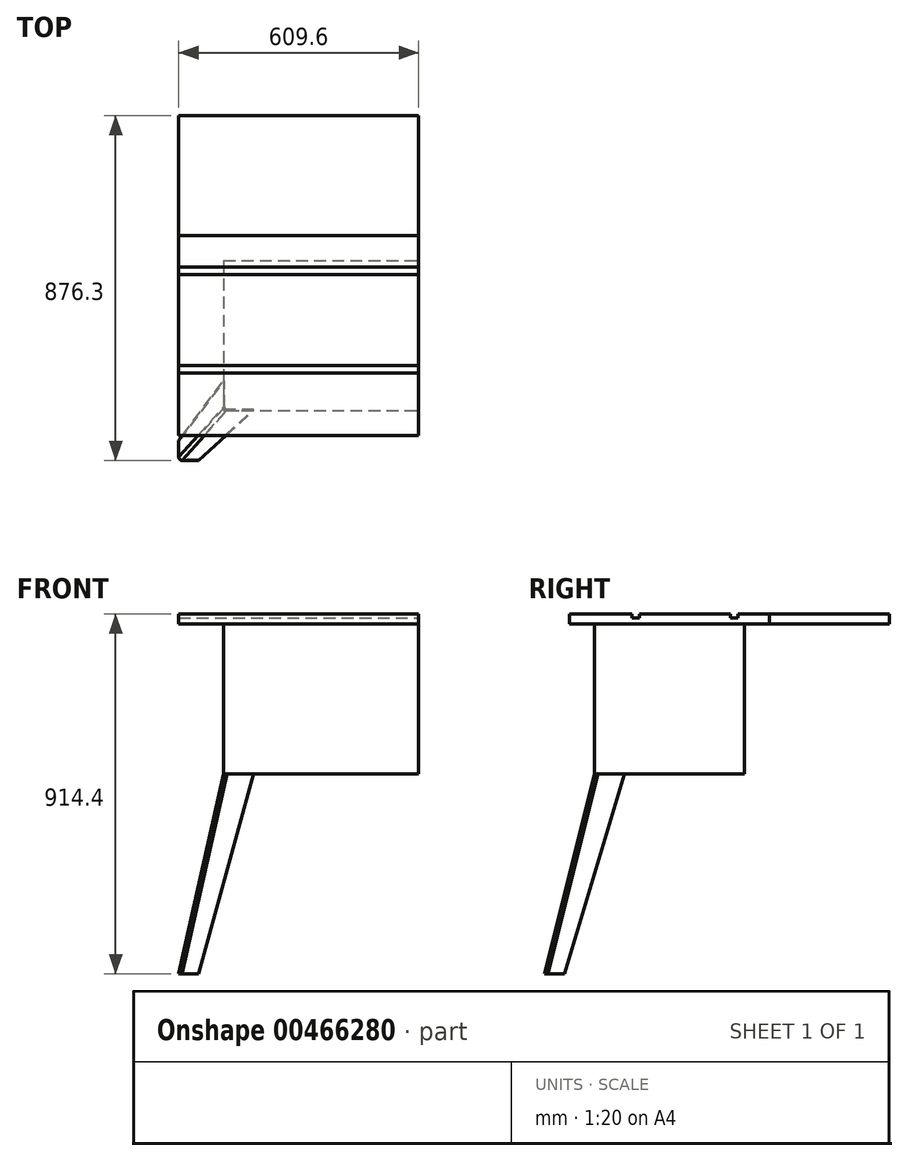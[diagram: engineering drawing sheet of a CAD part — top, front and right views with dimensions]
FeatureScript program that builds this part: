
annotation { "Feature Type Name" : "Feature", "Feature Type Description" : "" }
export const myFeature = defineFeature(function(context is Context, id is Id, definition is map)
    precondition{}
    {
        {
            var Q0;
            Q0=qCreatedBy(makeId("Top.planeOp"),FACE);
            var sketch = newSketch(context, id + "F0", { "sketchPlane" : qUnion([Q0])});
            skLineSegment(sketch, "E0", {"start": v(-361.95, -266.7) * mm, "end": v(-361.95, -308.61) * mm});
            skLineSegment(sketch, "E1", {"start": v(-353.06, -317.5) * mm, "end": v(-311.15, -317.5) * mm});
            skLineSegment(sketch, "E2", {"start": v(-311.15, -317.5) * mm, "end": v(-311.15, -314.96) * mm});
            skLineSegment(sketch, "E3", {"start": v(-311.15, -314.96) * mm, "end": v(-353.06, -314.96) * mm});
            skLineSegment(sketch, "E4", {"start": v(-359.41, -308.61) * mm, "end": v(-359.41, -266.7) * mm});
            skLineSegment(sketch, "E5", {"start": v(-359.41, -266.7) * mm, "end": v(-361.95, -266.7) * mm});
            skPoint(sketch, "E6.visualSharp", {"position": v(-359.41, -314.96) * mm});
            skArc(sketch, "E6.filletArc", {"start": v(-359.41, -308.61) * mm, "mid": v(-357.55, -313.1) * mm, "end": v(-353.06, -314.96) * mm});
            skPoint(sketch, "E7.visualSharp", {"position": v(-361.95, -317.5) * mm});
            skArc(sketch, "E7.filletArc", {"start": v(-361.95, -308.61) * mm, "mid": v(-359.35, -314.9) * mm, "end": v(-353.06, -317.5) * mm});
            skSolve(sketch);
        }
        {
            var Q0;
            Q0=qCreatedBy(makeId("Top.planeOp"),FACE);
            cPlane(context, id + "F1", {"entities" : qUnion([Q0]), "cplaneType" : CPlaneType.OFFSET, "offset" : 508 * mm, "width" : 152.4 * mm, "height" : 152.4 * mm});
        }
        {
            var Q0;
            Q0=qCreatedBy(id+"F1.planeOp",FACE);
            var sketch = newSketch(context, id + "F2", { "sketchPlane" : qUnion([Q0])});
            skPoint(sketch, "E8.middle", {"position": v(0, 0) * mm});
            skLineSegment(sketch, "E9", {"start": v(-247.65, -114.3) * mm, "end": v(-247.65, -181.61) * mm});
            skLineSegment(sketch, "E10", {"start": v(-238.76, -190.5) * mm, "end": v(-171.45, -190.5) * mm});
            skLineSegment(sketch, "E11", {"start": v(-171.45, -190.5) * mm, "end": v(-171.45, -187.96) * mm});
            skLineSegment(sketch, "E12", {"start": v(-171.45, -187.96) * mm, "end": v(-238.76, -187.96) * mm});
            skLineSegment(sketch, "E13", {"start": v(-245.11, -181.61) * mm, "end": v(-245.11, -114.3) * mm});
            skLineSegment(sketch, "E14", {"start": v(-245.11, -114.3) * mm, "end": v(-247.65, -114.3) * mm});
            skPoint(sketch, "E15.visualSharp", {"position": v(-245.11, -187.96) * mm});
            skArc(sketch, "E15.filletArc", {"start": v(-245.11, -181.61) * mm, "mid": v(-243.25, -186.1) * mm, "end": v(-238.76, -187.96) * mm});
            skPoint(sketch, "E16.visualSharp", {"position": v(-247.65, -190.5) * mm});
            skArc(sketch, "E16.filletArc", {"start": v(-247.65, -181.61) * mm, "mid": v(-245.05, -187.9) * mm, "end": v(-238.76, -190.5) * mm});
            skSolve(sketch);
        }
        {
            var Q0;
            Q0=makeQuery(id+"F0.imprint","IMPRINT",FACE,{"disambiguationData":[TD([[makeQuery(id+"F0.imprint","IMPRINT",EDGE,{"derivedFrom":sQuery(id+"F0.wireOp",EDGE,"E0")}),1.0]])]});
            var Q1;
            Q1=makeQuery(id+"F2.imprint","IMPRINT",FACE,{"disambiguationData":[TD([[makeQuery(id+"F2.imprint","IMPRINT",EDGE,{"derivedFrom":sQuery(id+"F2.wireOp",EDGE,"E9")}),1.0]])]});
            loft(context, id + "F3", {"sheetProfilesArray" : [{ "sheetProfileEntities" : qUnion([Q0]) }, { "sheetProfileEntities" : qUnion([Q1]) }]});
        }
        {
            var Q0;
            Q0=qCreatedBy(id+"F1.planeOp",FACE);
            var sketch = newSketch(context, id + "F4", { "sketchPlane" : qUnion([Q0])});
            skLineSegment(sketch, "E17.bottom", {"start": v(-247.65, 190.5) * mm, "end": v(247.65, 190.5) * mm});
            skLineSegment(sketch, "E17.top", {"start": v(-247.65, -190.5) * mm, "end": v(247.65, -190.5) * mm});
            skLineSegment(sketch, "E17.left", {"start": v(-247.65, 190.5) * mm, "end": v(-247.65, -190.5) * mm});
            skLineSegment(sketch, "E17.right", {"start": v(247.65, 190.5) * mm, "end": v(247.65, -190.5) * mm});
            skPoint(sketch, "E17.middle", {"position": v(0, 0) * mm});
            skSolve(sketch);
        }
        {
            var Q0;
            Q0=makeQuery(id+"F4.imprint","IMPRINT",FACE,{"disambiguationData":[TD([[makeQuery(id+"F4.imprint","IMPRINT",EDGE,{"derivedFrom":sQuery(id+"F4.wireOp",EDGE,"E17.bottom")}),-1.0]])]});
            extrude(context, id + "F5", {"entities" : qUnion([Q0]), "depth" : 381 * mm});
        }
        {
            var Q0;
            Q0=makeQuery(id+"F5.opExtrude","CAP_FACE",FACE,{"disambiguationData":[OSD([sQuery(id+"F4.wireOp",EDGE,"E17.bottom"),sQuery(id+"F4.wireOp",EDGE,"E17.top"),sQuery(id+"F4.wireOp",EDGE,"E17.left"),sQuery(id+"F4.wireOp",EDGE,"E17.right")])],"isStart":false});
            var sketch = newSketch(context, id + "F6", { "sketchPlane" : qUnion([Q0])});
            skLineSegment(sketch, "E18.bottom", {"start": v(247.65, 254) * mm, "end": v(-361.95, 254) * mm});
            skLineSegment(sketch, "E18.top", {"start": v(247.65, -254) * mm, "end": v(-361.95, -254) * mm});
            skLineSegment(sketch, "E18.left", {"start": v(247.65, 254) * mm, "end": v(247.65, -254) * mm});
            skLineSegment(sketch, "E18.right", {"start": v(-361.95, 254) * mm, "end": v(-361.95, -254) * mm});
            skLineSegment(sketch, "E19.bottom", {"start": v(-361.95, -254) * mm, "end": v(247.65, -254) * mm});
            skLineSegment(sketch, "E19.top", {"start": v(-361.95, -558.8) * mm, "end": v(247.65, -558.8) * mm});
            skLineSegment(sketch, "E19.left", {"start": v(-361.95, -254) * mm, "end": v(-361.95, -558.8) * mm});
            skLineSegment(sketch, "E19.right", {"start": v(247.65, -254) * mm, "end": v(247.65, -558.8) * mm});
            skLineSegment(sketch, "E20.top", {"start": v(247.65, 558.8) * mm, "end": v(-361.95, 558.8) * mm});
            skLineSegment(sketch, "E20.left", {"start": v(247.65, 254) * mm, "end": v(247.65, 558.8) * mm});
            skLineSegment(sketch, "E20.right", {"start": v(-361.95, 254) * mm, "end": v(-361.95, 558.8) * mm});
            skSolve(sketch);
        }
        {
            var Q0;
            Q0=makeQuery(id+"F6.imprint","IMPRINT",FACE,{"disambiguationData":[TD([[makeQuery(id+"F6.imprint","IMPRINT",EDGE,{"derivedFrom":sQuery(id+"F6.wireOp",EDGE,"E18.right")}),1.0]])]});
            var Q1;
            {var subQ1=makeQuery(id+"F5.opExtrude","CAP_EDGE",EDGE,{"disambiguationData":[OSD([sQuery(id+"F4.wireOp",EDGE,"E17.bottom")])],"isStart":false});Q1=makeQuery(id+"F6.imprint","IMPRINT",FACE,{"disambiguationData":[TD([[makeQuery(id+"F6.imprint","IMPRINT",EDGE,{"derivedFrom":subQ1}),-1.0]])]});}
            extrude(context, id + "F7", {"entities" : qUnion([Q0, Q1]), "depth" : 25.4 * mm});
        }
        {
            var Q0;
            Q0=makeQuery(id+"F6.imprint","IMPRINT",FACE,{"disambiguationData":[TD([[makeQuery(id+"F6.imprint","IMPRINT",EDGE,{"derivedFrom":sQuery(id+"F6.wireOp",EDGE,"E19.bottom")}),-1.0]])]});
            var Q1;
            Q1=makeQuery(id+"F6.imprint","IMPRINT",FACE,{"disambiguationData":[TD([[makeQuery(id+"F6.imprint","IMPRINT",EDGE,{"derivedFrom":sQuery(id+"F6.wireOp",EDGE,"E18.bottom")}),-1.0]])]});
            extrude(context, id + "F8", {"entities" : qUnion([Q0, Q1]), "depth" : 25.4 * mm});
        }
        {
            var Q0;
            Q0=makeQuery(id+"F7.opExtrude","CAP_FACE",FACE,{"disambiguationData":[OSD([sQuery(id+"F6.wireOp",EDGE,"E18.left"),sQuery(id+"F6.wireOp",EDGE,"E18.right"),sQuery(id+"F6.wireOp",EDGE,"E19.bottom"),sQuery(id+"F6.wireOp",EDGE,"E18.bottom")])],"isStart":false});
            var sketch = newSketch(context, id + "F9", { "sketchPlane" : qUnion([Q0])});
            skLineSegment(sketch, "E21.bottom", {"start": v(-361.95, 174) * mm, "end": v(247.65, 174) * mm});
            skLineSegment(sketch, "E21.top", {"start": v(-361.95, 154.95) * mm, "end": v(247.65, 154.95) * mm});
            skLineSegment(sketch, "E21.left", {"start": v(-361.95, 174) * mm, "end": v(-361.95, 154.95) * mm});
            skLineSegment(sketch, "E21.right", {"start": v(247.65, 174) * mm, "end": v(247.65, 154.95) * mm});
            skLineSegment(sketch, "E22.bottom", {"start": v(-361.95, -95.05) * mm, "end": v(247.65, -95.05) * mm});
            skLineSegment(sketch, "E22.top", {"start": v(-361.95, -76) * mm, "end": v(247.65, -76) * mm});
            skLineSegment(sketch, "E22.left", {"start": v(-361.95, -95.05) * mm, "end": v(-361.95, -76) * mm});
            skLineSegment(sketch, "E22.right", {"start": v(247.65, -95.05) * mm, "end": v(247.65, -76) * mm});
            skSolve(sketch);
        }
        {
            var Q0;
            Q0=makeQuery(id+"F9.imprint","IMPRINT",FACE,{"disambiguationData":[TD([[makeQuery(id+"F9.imprint","IMPRINT",EDGE,{"derivedFrom":sQuery(id+"F9.wireOp",EDGE,"E22.bottom")}),1.0]])]});
            var Q1;
            Q1=makeQuery(id+"F9.imprint","IMPRINT",FACE,{"disambiguationData":[TD([[makeQuery(id+"F9.imprint","IMPRINT",EDGE,{"derivedFrom":sQuery(id+"F9.wireOp",EDGE,"E21.bottom")}),-1.0]])]});
            extrude(context, id + "F10", {"entities" : qUnion([Q0, Q1]), "operationType" : NewBodyOperationType.REMOVE, "oppositeDirection" : true, "depth" : 9.52 * mm});
        }
    });
